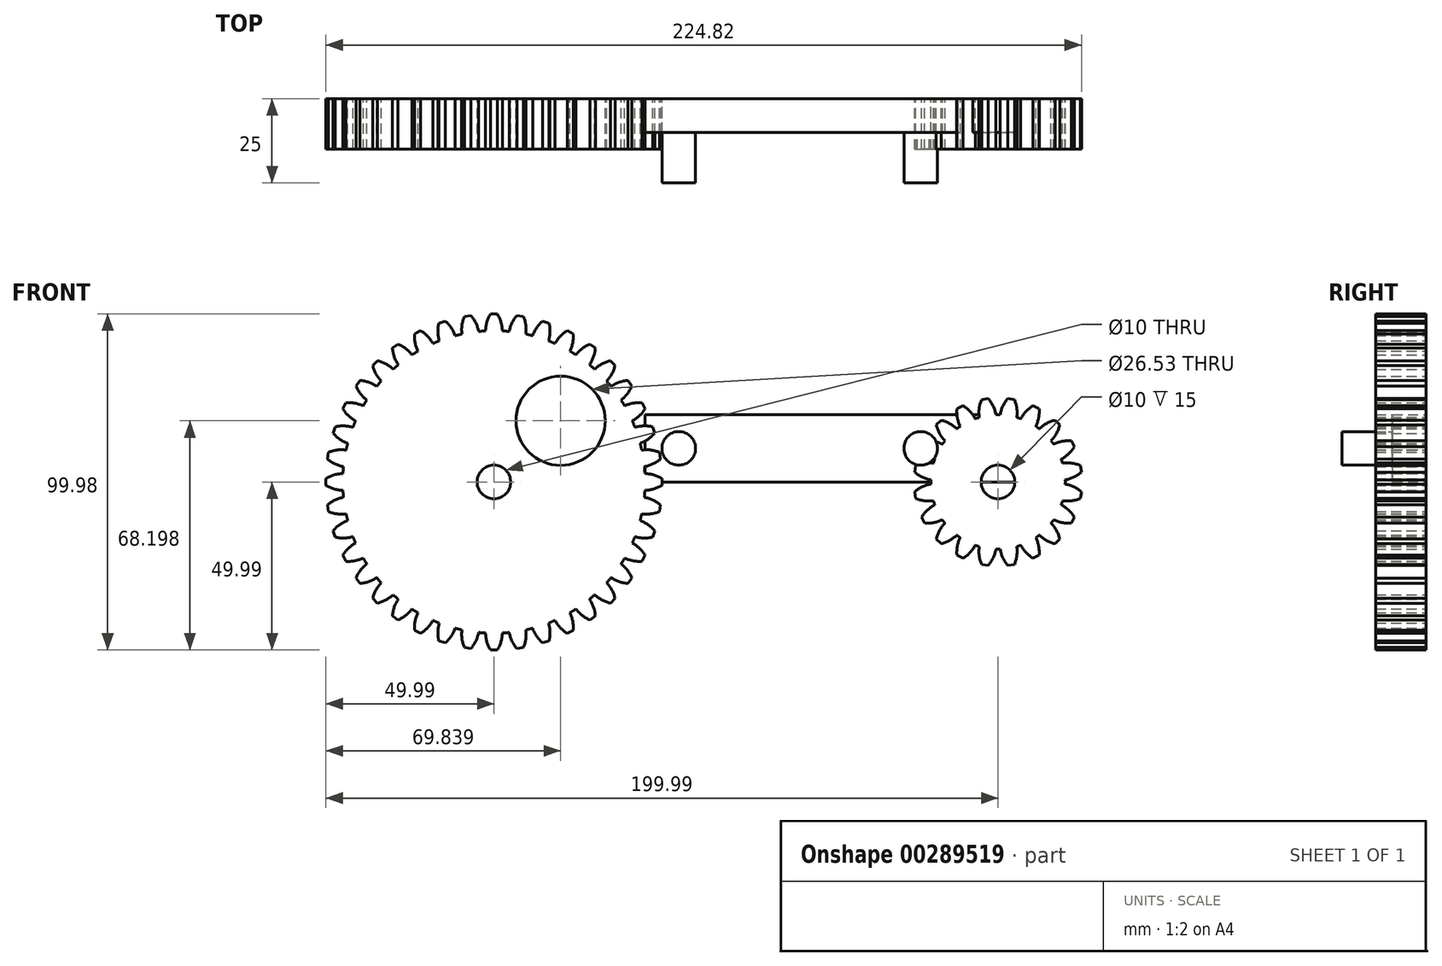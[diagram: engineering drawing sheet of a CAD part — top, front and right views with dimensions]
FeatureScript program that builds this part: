
annotation { "Feature Type Name" : "Feature", "Feature Type Description" : "" }
export const myFeature = defineFeature(function(context is Context, id is Id, definition is map)
    precondition{}
    {
        {
            var Q0;
            Q0=qCreatedBy(makeId("Front.planeOp"),FACE);
            var sketch = newSketch(context, id + "F0", { "sketchPlane" : qUnion([Q0])});
            skLineSegment(sketch, "E0.bottom", {"start": v(-55, 20) * mm, "end": v(55, 20) * mm});
            skLineSegment(sketch, "E0.top", {"start": v(-55, 0) * mm, "end": v(55, 0) * mm});
            skLineSegment(sketch, "E0.left", {"start": v(-55, 20) * mm, "end": v(-55, 0) * mm});
            skLineSegment(sketch, "E0.right", {"start": v(55, 20) * mm, "end": v(55, 0) * mm});
            skCircle(sketch, "E1", {"center": v(-45, 10) * mm, "radius": 5 * mm});
            skCircle(sketch, "E2", {"center": v(27, 10) * mm, "radius": 5 * mm});
            skPoint(sketch, "E3", {"position": v(0, 0) * mm});
            skSolve(sketch);
        }
        {
            var Q0;
            Q0=makeQuery(id+"F0.imprint","IMPRINT",FACE,{"disambiguationData":[TD([[makeQuery(id+"F0.imprint","IMPRINT",EDGE,{"derivedFrom":sQuery(id+"F0.wireOp",EDGE,"E0.bottom")}),-1.0]])]});
            extrude(context, id + "F1", {"entities" : qUnion([Q0]), "depth" : 10 * mm});
        }
        {
            var Q0;
            Q0=makeQuery(id+"F0.imprint","IMPRINT",FACE,{"disambiguationData":[TD([[makeQuery(id+"F0.imprint","IMPRINT",EDGE,{"derivedFrom":sQuery(id+"F0.wireOp",EDGE,"E1")}),1.0]])]});
            var Q1;
            Q1=makeQuery(id+"F0.imprint","IMPRINT",FACE,{"disambiguationData":[TD([[makeQuery(id+"F0.imprint","IMPRINT",EDGE,{"derivedFrom":sQuery(id+"F0.wireOp",EDGE,"E2")}),1.0]])]});
            extrude(context, id + "F2", {"entities" : qUnion([Q0, Q1]), "operationType" : NewBodyOperationType.ADD, "depth" : 25 * mm});
        }
        {
            var Q0;
            Q0=qCreatedBy(makeId("Front.planeOp"),FACE);
            var sketch = newSketch(context, id + "F3", { "sketchPlane" : qUnion([Q0])});
            skCircle(sketch, "E4", {"center": v(-100, 0) * mm, "radius": 45 * mm});
            skCircle(sketch, "E5", {"center": v(-100, 0) * mm, "radius": 5 * mm});
            skCircle(sketch, "E6", {"center": v(50, 0) * mm, "radius": 5 * mm});
            skCircle(sketch, "E7", {"center": v(50, 0) * mm, "radius": 20 * mm});
            skCircle(sketch, "E8", {"center": v(-100, 0) * mm, "radius": 50 * mm, "construction": true});
            skLineSegment(sketch, "E9", {"start": v(-100, 0) * mm, "end": v(-100, 50) * mm, "construction": true});
            skLineSegment(sketch, "E10", {"start": v(-101, 49.99) * mm, "end": v(-99, 49.99) * mm});
            skLineSegment(sketch, "E11", {"start": v(-102.5, 44.93) * mm, "end": v(-97.5, 44.93) * mm, "construction": true});
            skLineSegment(sketch, "E12", {"start": v(-102.5, 44.93) * mm, "end": v(-101, 49.99) * mm, "construction": true});
            skLineSegment(sketch, "E13", {"start": v(-99, 49.99) * mm, "end": v(-97.5, 44.93) * mm, "construction": true});
            skArc(sketch, "E14", {"start": v(-101, 49.99) * mm, "mid": v(-102.09, 47.56) * mm, "end": v(-102.5, 44.93) * mm});
            skArc(sketch, "E15", {"start": v(-97.5, 44.93) * mm, "mid": v(-97.91, 47.56) * mm, "end": v(-99, 49.99) * mm});
            skLineSegment(sketch, "E16", {"start": v(-100, 0) * mm, "end": v(0, 0) * mm, "construction": true});
            skLineSegment(sketch, "E17", {"start": v(0, 0) * mm, "end": v(50, 0) * mm, "construction": true});
            skCircle(sketch, "E18", {"center": v(50, 0) * mm, "radius": 25 * mm, "construction": true});
            skLineSegment(sketch, "E19", {"start": v(50, 0) * mm, "end": v(67.68, 17.68) * mm, "construction": true});
            skLineSegment(sketch, "E20", {"start": v(62.26, 15.8) * mm, "end": v(65.8, 12.26) * mm, "construction": true});
            skLineSegment(sketch, "E21", {"start": v(66.96, 18.37) * mm, "end": v(68.37, 16.96) * mm});
            skArc(sketch, "E22", {"start": v(66.96, 18.37) * mm, "mid": v(64.43, 17.4) * mm, "end": v(62.26, 15.8) * mm});
            skArc(sketch, "E23", {"start": v(65.8, 12.26) * mm, "mid": v(67.4, 14.43) * mm, "end": v(68.37, 16.96) * mm});
            skCircle(sketch, "E24", {"center": v(-80.15, 18.2) * mm, "radius": 13.26 * mm});
            skLineSegment(sketch, "E25", {"start": v(50, 0) * mm, "end": v(50, 25) * mm, "construction": true});
            skSolve(sketch);
        }
        {
            var Q0;
            Q0=makeQuery(id+"F3.imprint","IMPRINT",FACE,{"disambiguationData":[TD([[makeQuery(id+"F3.imprint","IMPRINT",EDGE,{"derivedFrom":sQuery(id+"F3.wireOp",EDGE,"E5")}),-1.0]])]});
            var Q1;
            Q1 = qBodyType(qCreatedBy(id + "FsXEAtgqO9TnXvs_3" ,FACE), BodyType.SOLID);
            extrude(context, id + "F4", {"entities" : qUnion([Q0]), "endBoundEntityFace" : qUnion([Q1]), "depth" : 15 * mm});
        }
        {
            var Q0;
            Q0=makeQuery(id+"F3.imprint","IMPRINT",FACE,{"disambiguationData":[TD([[makeQuery(id+"F3.imprint","IMPRINT",EDGE,{"derivedFrom":sQuery(id+"F3.wireOp",EDGE,"E10")}),-1.0]])]});
            var Q1;
            Q1=qCreatedBy(id+"FsXEAtgqO9TnXvs_3.planeOp",FACE);
            extrude(context, id + "F5", {"entities" : qUnion([Q0]), "endBoundEntityFace" : qUnion([Q1]), "depth" : 15 * mm});
        }
        {
            var Q0;
            Q0=makeQuery(id+"F5.opExtrude","SWEPT_BODY",BODY,{"disambiguationData":[OSD([sQuery(id+"F3.wireOp",EDGE,"E4"),sQuery(id+"F3.wireOp",EDGE,"E10"),sQuery(id+"F3.wireOp",EDGE,"E14"),sQuery(id+"F3.wireOp",EDGE,"E15")])]});
            var Q1;
            Q1=sQuery(id+"F3.wireOp",EDGE,"E4");
            circularPattern(context, id + "F6", {"operationType" : NewBodyOperationType.ADD, "entities" : qUnion([Q0]), "axis" : qUnion([Q1]), "angle" : 360 * degree, "instanceCount" : 40, "equalSpace" : true});
        }
        {
            var Q0;
            Q0=makeQuery(id+"F3.imprint","IMPRINT",FACE,{"disambiguationData":[TD([[makeQuery(id+"F3.imprint","IMPRINT",EDGE,{"derivedFrom":sQuery(id+"F3.wireOp",EDGE,"E6")}),-1.0]])]});
            extrude(context, id + "F7", {"entities" : qUnion([Q0]), "depth" : 15 * mm});
        }
        {
            var Q0;
            Q0=makeQuery(id+"F3.imprint","IMPRINT",FACE,{"disambiguationData":[TD([[makeQuery(id+"F3.imprint","IMPRINT",EDGE,{"derivedFrom":sQuery(id+"F3.wireOp",EDGE,"E21")}),-1.0]])]});
            extrude(context, id + "F8", {"entities" : qUnion([Q0]), "depth" : 15 * mm});
        }
        {
            var Q0;
            Q0=makeQuery(id+"F8.opExtrude","SWEPT_BODY",BODY,{"disambiguationData":[OSD([sQuery(id+"F3.wireOp",EDGE,"E7"),sQuery(id+"F3.wireOp",EDGE,"E21"),sQuery(id+"F3.wireOp",EDGE,"E22"),sQuery(id+"F3.wireOp",EDGE,"E23")])]});
            var Q1;
            Q1=sQuery(id+"F3.wireOp",EDGE,"E7");
            circularPattern(context, id + "F9", {"operationType" : NewBodyOperationType.ADD, "entities" : qUnion([Q0]), "axis" : qUnion([Q1]), "angle" : 360 * degree, "instanceCount" : 20, "equalSpace" : true});
        }
    });
